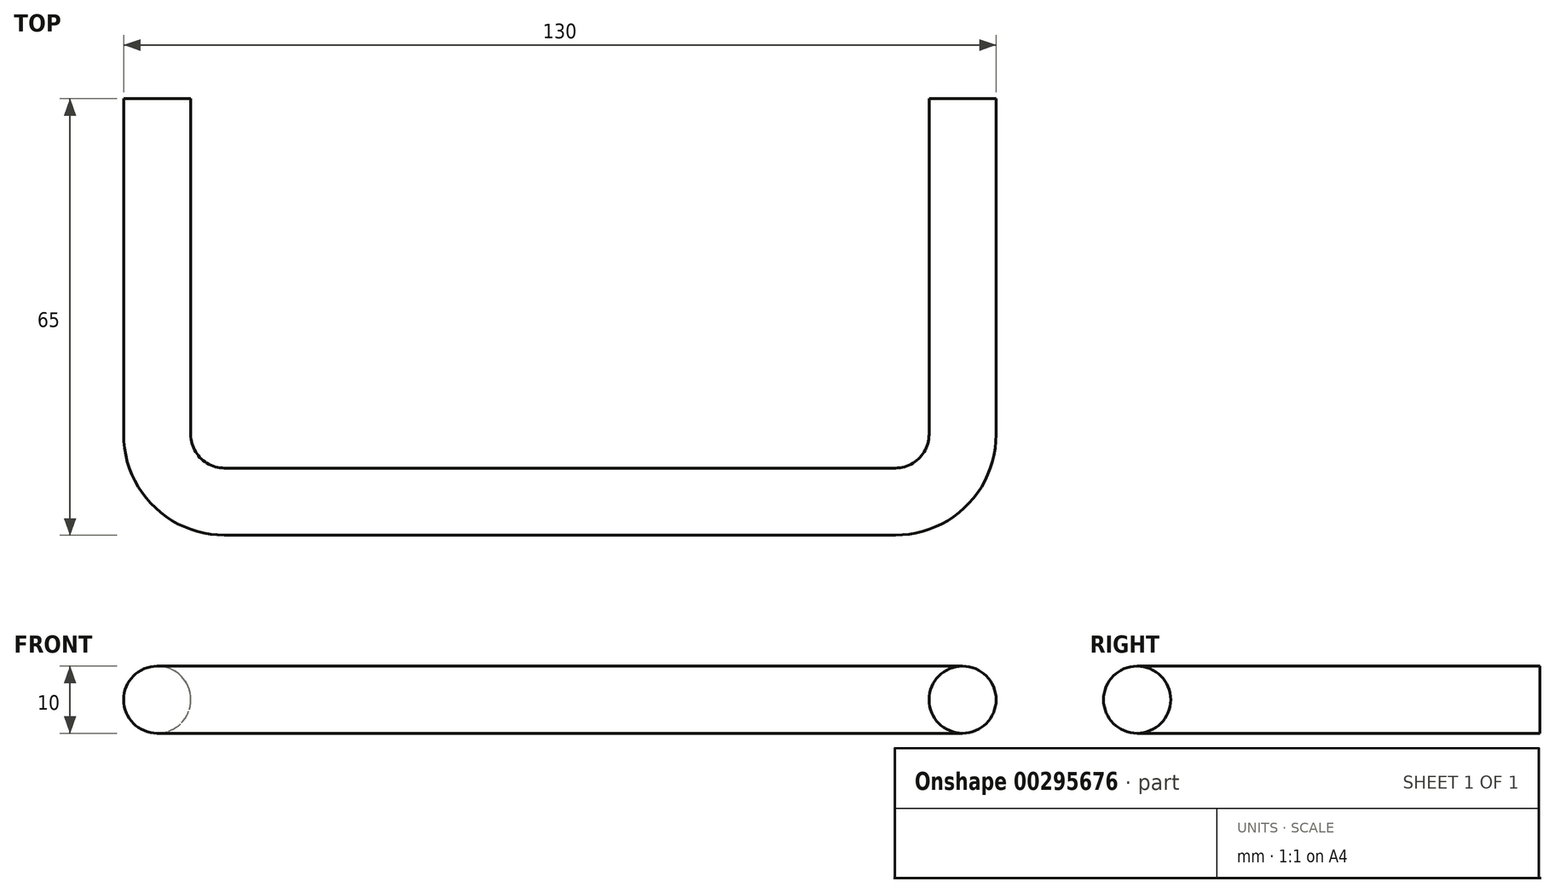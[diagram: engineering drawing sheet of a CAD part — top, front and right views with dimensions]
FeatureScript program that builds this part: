
annotation { "Feature Type Name" : "Feature", "Feature Type Description" : "" }
export const myFeature = defineFeature(function(context is Context, id is Id, definition is map)
    precondition{}
    {
        {
            var Q0;
            Q0=qCreatedBy(makeId("Top.planeOp"),FACE);
            var sketch = newSketch(context, id + "F0", { "sketchPlane" : qUnion([Q0])});
            skLineSegment(sketch, "E0", {"start": v(0, -27.69) * mm, "end": v(0, 30.6) * mm, "construction": true});
            skLineSegment(sketch, "E1", {"start": v(-44.86, 0) * mm, "end": v(43.22, 0) * mm, "construction": true});
            skLineSegment(sketch, "E2", {"start": v(-60, 42.94) * mm, "end": v(-60, -7.06) * mm, "construction": true});
            skLineSegment(sketch, "E3", {"start": v(-50, -17.06) * mm, "end": v(0, -17.06) * mm, "construction": true});
            skLineSegment(sketch, "E4.MirrorCS", {"start": v(50, -17.06) * mm, "end": v(0, -17.06) * mm, "construction": true});
            skLineSegment(sketch, "E5.MirrorCS", {"start": v(60, 42.94) * mm, "end": v(60, -7.06) * mm, "construction": true});
            skPoint(sketch, "E6.visualSharp", {"position": v(-60, -17.06) * mm});
            skArc(sketch, "E6.filletArc", {"start": v(-60, -7.06) * mm, "mid": v(-57.07, -14.13) * mm, "end": v(-50, -17.06) * mm, "construction": true});
            skPoint(sketch, "E7.visualSharp", {"position": v(60, -17.06) * mm});
            skArc(sketch, "E7.filletArc", {"start": v(50, -17.06) * mm, "mid": v(57.07, -14.13) * mm, "end": v(60, -7.06) * mm, "construction": true});
            skLineSegment(sketch, "E8.0", {"start": v(-65, 42.94) * mm, "end": v(-65, -7.06) * mm});
            skLineSegment(sketch, "E9.0", {"start": v(-55, 42.94) * mm, "end": v(-55, -7.06) * mm});
            skArc(sketch, "E10.0", {"start": v(-55, -7.06) * mm, "mid": v(-53.54, -10.6) * mm, "end": v(-50, -12.06) * mm});
            skArc(sketch, "E11.0", {"start": v(-65, -7.06) * mm, "mid": v(-60.6, -17.66) * mm, "end": v(-50, -22.06) * mm});
            skLineSegment(sketch, "E12.0", {"start": v(-50, -22.06) * mm, "end": v(0, -22.06) * mm});
            skLineSegment(sketch, "E13.0", {"start": v(-50, -12.06) * mm, "end": v(0, -12.06) * mm});
            skLineSegment(sketch, "E14.0", {"start": v(50, -12.06) * mm, "end": v(0, -12.06) * mm});
            skLineSegment(sketch, "E15.0", {"start": v(50, -22.06) * mm, "end": v(0, -22.06) * mm});
            skArc(sketch, "E16.0", {"start": v(50, -22.06) * mm, "mid": v(60.6, -17.66) * mm, "end": v(65, -7.06) * mm});
            skArc(sketch, "E17.0", {"start": v(50, -12.06) * mm, "mid": v(53.54, -10.6) * mm, "end": v(55, -7.06) * mm});
            skLineSegment(sketch, "E18.0", {"start": v(65, 42.94) * mm, "end": v(65, -7.06) * mm});
            skLineSegment(sketch, "E19.0", {"start": v(55, 42.94) * mm, "end": v(55, -7.06) * mm});
            skLineSegment(sketch, "E20", {"start": v(-65, 42.94) * mm, "end": v(-55, 42.94) * mm});
            skLineSegment(sketch, "E21", {"start": v(55, 42.94) * mm, "end": v(65, 42.94) * mm});
            skSolve(sketch);
        }
        {
            var Q0;
            Q0=makeQuery(id+"F0.imprint","IMPRINT",FACE,{"disambiguationData":[TD([[makeQuery(id+"F0.imprint","IMPRINT",EDGE,{"derivedFrom":sQuery(id+"F0.wireOp",EDGE,"E8.0")}),1.0]])]});
            extrude(context, id + "F1", {"entities" : qUnion([Q0]), "depth" : 10 * mm, "symmetric" : true});
        }
        {
            var Q0;
            Q0=makeQuery(id+"F1.opExtrude","CAP_EDGE",EDGE,{"disambiguationData":[OSD([sQuery(id+"F0.wireOp",EDGE,"E8.0")])],"isStart":false});
            var Q1;
            Q1=makeQuery(id+"F1.opExtrude","SWEPT_FACE",FACE,{"disambiguationData":[OSD([sQuery(id+"F0.wireOp",EDGE,"E11.0")])]});
            var Q2;
            Q2=makeQuery(id+"F1.opExtrude","SWEPT_FACE",FACE,{"disambiguationData":[OSD([sQuery(id+"F0.wireOp",EDGE,"E12.0"),sQuery(id+"F0.wireOp",EDGE,"E15.0")])]});
            var Q3;
            Q3=makeQuery(id+"F1.opExtrude","SWEPT_FACE",FACE,{"disambiguationData":[OSD([sQuery(id+"F0.wireOp",EDGE,"E16.0")])]});
            var Q4;
            Q4=makeQuery(id+"F1.opExtrude","SWEPT_FACE",FACE,{"disambiguationData":[OSD([sQuery(id+"F0.wireOp",EDGE,"E17.0")])]});
            var Q5;
            Q5=makeQuery(id+"F1.opExtrude","SWEPT_FACE",FACE,{"disambiguationData":[OSD([sQuery(id+"F0.wireOp",EDGE,"E13.0"),sQuery(id+"F0.wireOp",EDGE,"E14.0")])]});
            var Q6;
            Q6=makeQuery(id+"F1.opExtrude","SWEPT_FACE",FACE,{"disambiguationData":[OSD([sQuery(id+"F0.wireOp",EDGE,"E10.0")])]});
            fillet(context, id + "F2", {"entities" : qUnion([Q0, Q1, Q2, Q3, Q4, Q5, Q6]), "radius" : 5 * mm, "tangentPropagation" : true, "allowEdgeOverflow" : false});
        }
    });
